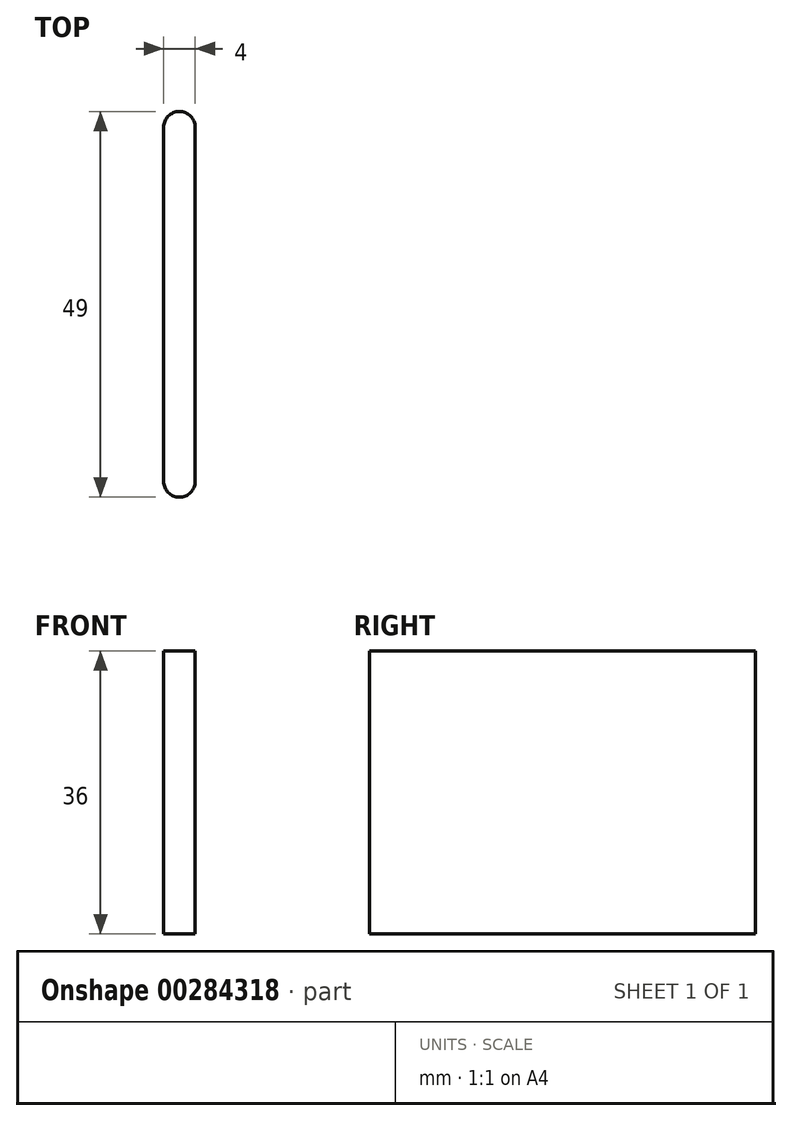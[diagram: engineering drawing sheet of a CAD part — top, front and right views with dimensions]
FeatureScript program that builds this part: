
annotation { "Feature Type Name" : "Feature", "Feature Type Description" : "" }
export const myFeature = defineFeature(function(context is Context, id is Id, definition is map)
    precondition{}
    {
        {
            var Q0;
            Q0=qCreatedBy(makeId("Top.planeOp"),FACE);
            var sketch = newSketch(context, id + "F0", { "sketchPlane" : qUnion([Q0])});
            skArc(sketch, "E0", {"start": v(2, 22.4) * mm, "mid": v(0, 24.4) * mm, "end": v(-2, 22.4) * mm});
            skArc(sketch, "E1", {"start": v(-2, -22.6) * mm, "mid": v(0, -24.6) * mm, "end": v(2, -22.6) * mm});
            skLineSegment(sketch, "E2", {"start": v(2, 22.4) * mm, "end": v(2, -22.6) * mm});
            skLineSegment(sketch, "E3", {"start": v(-2, 22.4) * mm, "end": v(-2, -22.6) * mm});
            skSolve(sketch);
        }
        {
            var Q0;
            Q0=makeQuery(id+"F0.imprint","IMPRINT",FACE,{"disambiguationData":[TD([[makeQuery(id+"F0.imprint","IMPRINT",EDGE,{"derivedFrom":sQuery(id+"F0.wireOp",EDGE,"E0")}),1.0]])]});
            extrude(context, id + "F1", {"entities" : qUnion([Q0]), "depth" : 36 * mm, "symmetric" : true});
        }
    });
